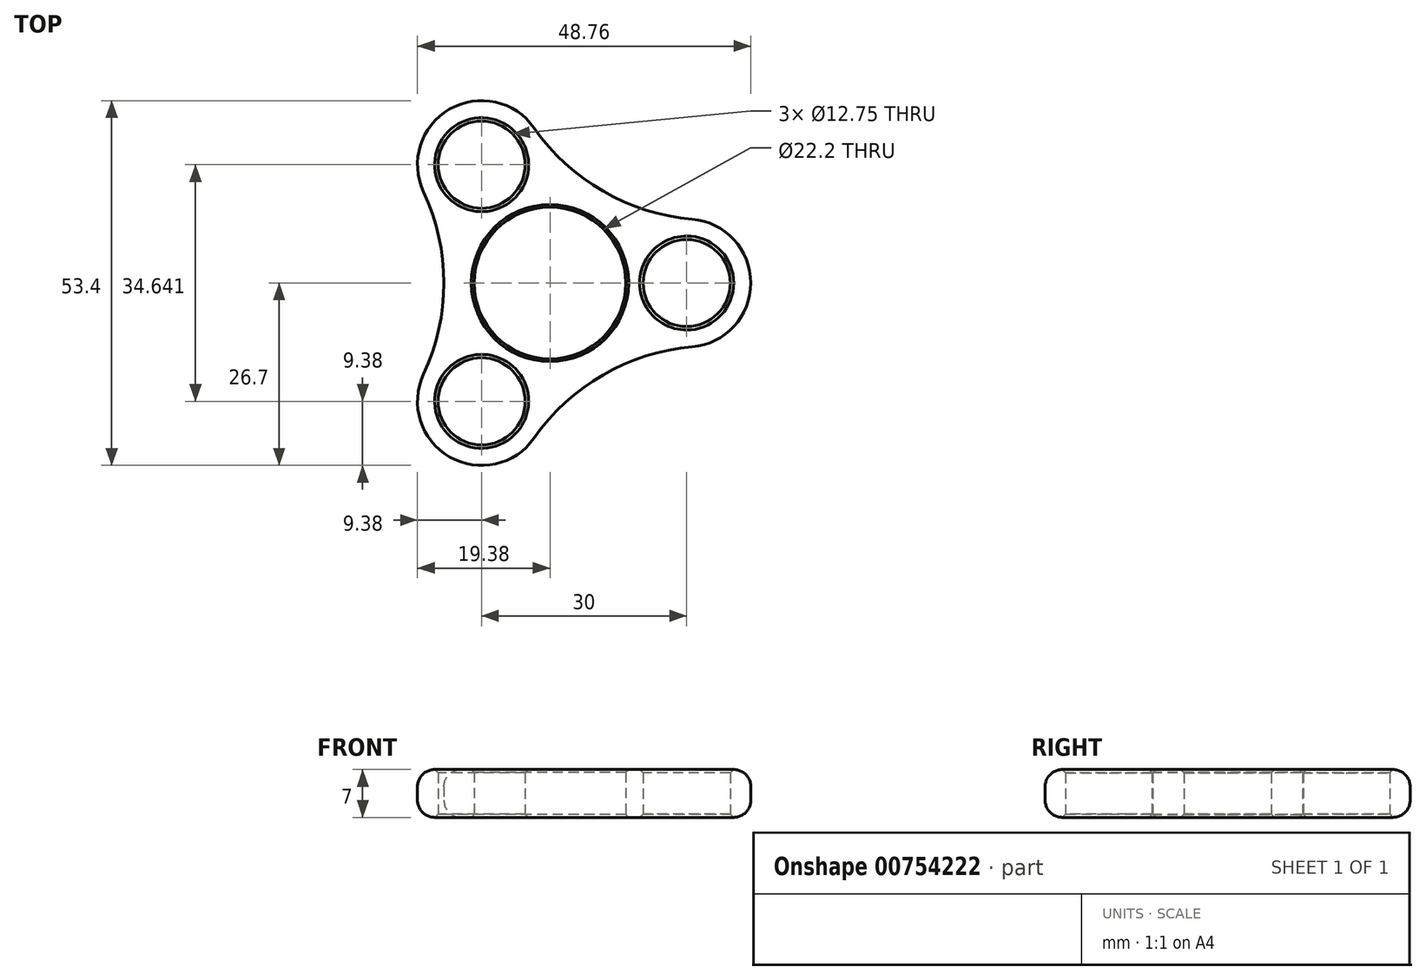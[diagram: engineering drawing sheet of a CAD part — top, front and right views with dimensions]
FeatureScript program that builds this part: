
annotation { "Feature Type Name" : "Feature", "Feature Type Description" : "" }
export const myFeature = defineFeature(function(context is Context, id is Id, definition is map)
    precondition{}
    {
        {
            var Q0;
            Q0=qCreatedBy(makeId("Top.planeOp"),FACE);
            var sketch = newSketch(context, id + "F0", { "sketchPlane" : qUnion([Q0])});
            skCircle(sketch, "E0", {"center": v(0, 0) * mm, "radius": 11.1 * mm});
            skPoint(sketch, "E1", {"position": v(20, 0) * mm});
            skCircle(sketch, "E2", {"center": v(20, 0) * mm, "radius": 6.38 * mm});
            skArc(sketch, "E3.0", {"start": v(20.8, -9.34) * mm, "mid": v(29.38, 0) * mm, "end": v(20.8, 9.34) * mm});
            skArc(sketch, "E4.1.0", {"start": v(-2.3, 22.68) * mm, "mid": v(-14.69, 25.44) * mm, "end": v(-18.49, 13.34) * mm});
            skCircle(sketch, "E4.1.1", {"center": v(-10, 17.32) * mm, "radius": 6.38 * mm});
            skArc(sketch, "E4.2.0", {"start": v(-18.49, -13.34) * mm, "mid": v(-14.69, -25.44) * mm, "end": v(-2.3, -22.68) * mm});
            skCircle(sketch, "E4.2.1", {"center": v(-10, -17.32) * mm, "radius": 6.38 * mm});
            skArc(sketch, "E5", {"start": v(20.8, -9.34) * mm, "mid": v(7.76, -13.44) * mm, "end": v(-2.3, -22.68) * mm});
            skArc(sketch, "E6.1.0", {"start": v(-2.3, 22.68) * mm, "mid": v(7.76, 13.44) * mm, "end": v(20.8, 9.34) * mm});
            skArc(sketch, "E6.2.0", {"start": v(-18.49, -13.34) * mm, "mid": v(-15.51, 0) * mm, "end": v(-18.49, 13.34) * mm});
            skSolve(sketch);
        }
        {
            var Q0;
            Q0=makeQuery(id+"F0.imprint","IMPRINT",FACE,{"disambiguationData":[TD([[makeQuery(id+"F0.imprint","IMPRINT",EDGE,{"derivedFrom":sQuery(id+"F0.wireOp",EDGE,"E4.1.1")}),-1.0]])]});
            var Q1;
            {var subQ0=sQuery(id+"F0.wireOp",EDGE,"ymMV7DUU-YaXF-13PJ-Upio-JPY2yyDOcRfn");var subQ1=sQuery(id+"F0.wireOp",EDGE,"e07e0217-3c4f-4238-9027-1b7dd3b318d3.0");var subQ2=makeQuery(id+"F0.imprint","INTERSECT",VERTEX,{"derivedFrom":[subQ1,subQ0]});Q1=makeQuery(id+"F0.imprint","IMPRINT",FACE,{"disambiguationData":[TD([[makeQuery(id+"F0.imprint","IMPRINT",EDGE,{"disambiguationData":[TD([[subQ2,1.0]])],"derivedFrom":subQ1}),-1.0]])]});}
            var Q2;
            Q2=makeQuery(id+"F0.imprint","IMPRINT",FACE,{"disambiguationData":[TD([[makeQuery(id+"F0.imprint","IMPRINT",EDGE,{"derivedFrom":sQuery(id+"F0.wireOp",EDGE,"E0")}),-1.0]])]});
            var Q3;
            {var subQ0=sQuery(id+"F0.wireOp",EDGE,"ymMV7DUU-YaXF-13PJ-Upio-JPY2yyDOcRfn");var subQ1=sQuery(id+"F0.wireOp",EDGE,"e07e0217-3c4f-4238-9027-1b7dd3b318d3.0");var subQ2=makeQuery(id+"F0.imprint","INTERSECT",VERTEX,{"derivedFrom":[subQ1,subQ0]});Q3=makeQuery(id+"F0.imprint","IMPRINT",FACE,{"disambiguationData":[TD([[makeQuery(id+"F0.imprint","IMPRINT",EDGE,{"disambiguationData":[TD([[subQ2,-1.0]])],"derivedFrom":subQ1}),-1.0]])]});}
            var Q4;
            Q4=makeQuery(id+"F0.imprint","IMPRINT",FACE,{"disambiguationData":[TD([[makeQuery(id+"F0.imprint","IMPRINT",EDGE,{"derivedFrom":sQuery(id+"F0.wireOp",EDGE,"E2")}),-1.0]])]});
            var Q5;
            {var subQ0=sQuery(id+"F0.wireOp",EDGE,"NfNrvnus-3jaq-3huT-B7Wp-5CzjeCRbWqY2");var subQ1=sQuery(id+"F0.wireOp",EDGE,"e07e0217-3c4f-4238-9027-1b7dd3b318d3.0");var subQ2=makeQuery(id+"F0.imprint","INTERSECT",VERTEX,{"derivedFrom":[subQ1,subQ0]});Q5=makeQuery(id+"F0.imprint","IMPRINT",FACE,{"disambiguationData":[TD([[makeQuery(id+"F0.imprint","IMPRINT",EDGE,{"disambiguationData":[TD([[subQ2,1.0]])],"derivedFrom":subQ1}),-1.0]])]});}
            var Q6;
            Q6=makeQuery(id+"F0.imprint","IMPRINT",FACE,{"disambiguationData":[TD([[makeQuery(id+"F0.imprint","IMPRINT",EDGE,{"derivedFrom":sQuery(id+"F0.wireOp",EDGE,"E4.2.1")}),-1.0]])]});
            extrude(context, id + "F1", {"entities" : qUnion([Q0, Q1, Q2, Q3, Q4, Q5, Q6]), "depth" : 7 * mm, "offsetDistance" : 25 * mm});
        }
        {
            var Q0;
            Q0=makeQuery(id+"F1.opExtrude","CAP_EDGE",EDGE,{"disambiguationData":[OSD([sQuery(id+"F0.wireOp",EDGE,"E5")])],"isStart":true});
            var Q1;
            Q1=makeQuery(id+"F1.opExtrude","CAP_EDGE",EDGE,{"disambiguationData":[OSD([sQuery(id+"F0.wireOp",EDGE,"E5")])],"isStart":false});
            fillet(context, id + "F2", {"entities" : qUnion([Q0, Q1]), "radius" : 2.5 * mm, "tangentPropagation" : true, "allowEdgeOverflow" : false});
        }
        {
            var Q0;
            Q0=makeQuery(id+"F1.opExtrude","CAP_EDGE",EDGE,{"disambiguationData":[OSD([sQuery(id+"F0.wireOp",EDGE,"E0")])],"isStart":false});
            var Q1;
            Q1=makeQuery(id+"F1.opExtrude","CAP_EDGE",EDGE,{"disambiguationData":[OSD([sQuery(id+"F0.wireOp",EDGE,"E0")])],"isStart":true});
            chamfer(context, id + "F3", {"entities" : qUnion([Q0, Q1]), "width" : 0.4 * mm, "tangentPropagation" : true});
        }
        {
            var Q0;
            Q0=makeQuery(id+"F1.opExtrude","CAP_EDGE",EDGE,{"disambiguationData":[OSD([sQuery(id+"F0.wireOp",EDGE,"E4.1.1")])],"isStart":false});
            var Q1;
            Q1=makeQuery(id+"F1.opExtrude","CAP_EDGE",EDGE,{"disambiguationData":[OSD([sQuery(id+"F0.wireOp",EDGE,"E4.1.1")])],"isStart":true});
            var Q2;
            Q2=makeQuery(id+"F1.opExtrude","CAP_EDGE",EDGE,{"disambiguationData":[OSD([sQuery(id+"F0.wireOp",EDGE,"E4.2.1")])],"isStart":true});
            var Q3;
            Q3=makeQuery(id+"F1.opExtrude","CAP_EDGE",EDGE,{"disambiguationData":[OSD([sQuery(id+"F0.wireOp",EDGE,"E4.2.1")])],"isStart":false});
            var Q4;
            Q4=makeQuery(id+"F1.opExtrude","CAP_EDGE",EDGE,{"disambiguationData":[OSD([sQuery(id+"F0.wireOp",EDGE,"E2")])],"isStart":true});
            var Q5;
            Q5=makeQuery(id+"F1.opExtrude","CAP_EDGE",EDGE,{"disambiguationData":[OSD([sQuery(id+"F0.wireOp",EDGE,"E2")])],"isStart":false});
            chamfer(context, id + "F4", {"entities" : qUnion([Q0, Q1, Q2, Q3, Q4, Q5]), "width" : 0.5 * mm, "tangentPropagation" : true});
        }
    });
